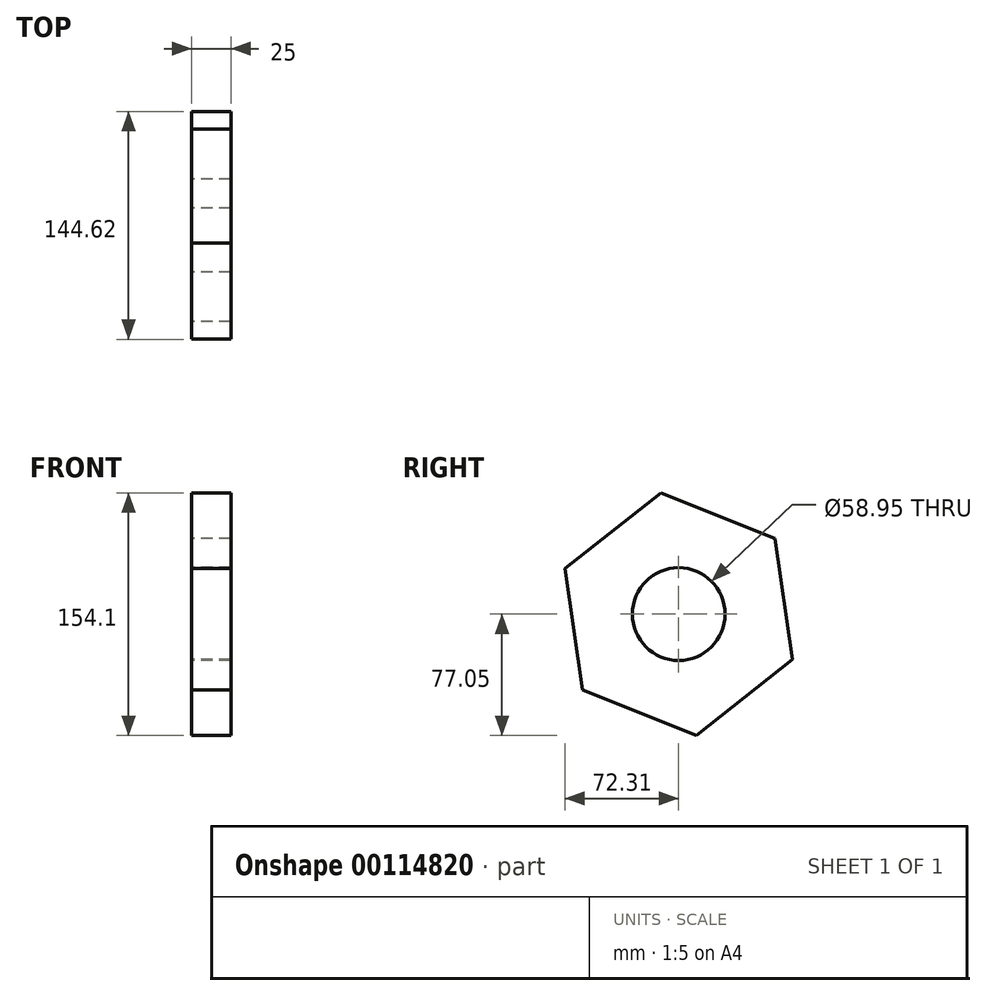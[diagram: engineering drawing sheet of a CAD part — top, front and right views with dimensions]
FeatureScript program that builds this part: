
annotation { "Feature Type Name" : "Feature", "Feature Type Description" : "" }
export const myFeature = defineFeature(function(context is Context, id is Id, definition is map)
    precondition{}
    {
        {
            var Q0;
            Q0=qCreatedBy(makeId("Right.planeOp"),FACE);
            var sketch = newSketch(context, id + "F0", { "sketchPlane" : qUnion([Q0])});
            skCircle(sketch, "E0.cCircle", {"center": v(0, 0) * mm, "radius": 67.42 * mm, "construction": true});
            skLineSegment(sketch, "E0.0", {"start": v(72.3, -28.86) * mm, "end": v(11.16, -77.05) * mm});
            skLineSegment(sketch, "E0.1", {"start": v(11.16, -77.05) * mm, "end": v(-61.15, -48.19) * mm});
            skLineSegment(sketch, "E0.2", {"start": v(-61.15, -48.19) * mm, "end": v(-72.3, 28.86) * mm});
            skLineSegment(sketch, "E0.3", {"start": v(-72.3, 28.86) * mm, "end": v(-11.16, 77.05) * mm});
            skLineSegment(sketch, "E0.4", {"start": v(-11.16, 77.05) * mm, "end": v(61.15, 48.19) * mm});
            skLineSegment(sketch, "E0.5", {"start": v(61.15, 48.19) * mm, "end": v(72.3, -28.86) * mm});
            skPoint(sketch, "E0.0.midPoint", {"position": v(41.73, -52.96) * mm});
            skCircle(sketch, "E1", {"center": v(0, 0) * mm, "radius": 29.47 * mm});
            skSolve(sketch);
        }
        {
            var Q0;
            Q0=makeQuery(id+"F0.imprint","IMPRINT",FACE,{"disambiguationData":[TD([[makeQuery(id+"F0.imprint","IMPRINT",EDGE,{"derivedFrom":sQuery(id+"F0.wireOp",EDGE,"E0.0")}),-1.0]])]});
            extrude(context, id + "F1", {"entities" : qUnion([Q0]), "depth" : 25 * mm});
        }
    });
